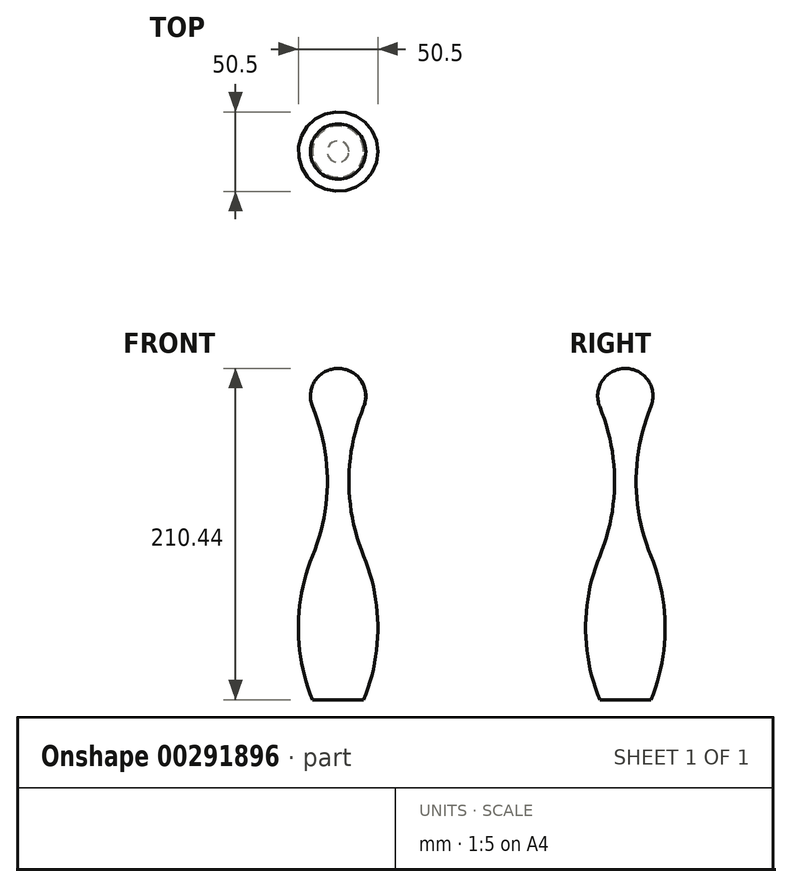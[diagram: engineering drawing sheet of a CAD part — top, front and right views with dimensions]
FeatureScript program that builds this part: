
annotation { "Feature Type Name" : "Feature", "Feature Type Description" : "" }
export const myFeature = defineFeature(function(context is Context, id is Id, definition is map)
    precondition{}
    {
        {
            var Q0;
            Q0=qCreatedBy(makeId("Front.planeOp"),FACE);
            var sketch = newSketch(context, id + "F0", { "sketchPlane" : qUnion([Q0])});
            skLineSegment(sketch, "E0", {"start": v(0, 0) * mm, "end": v(25, 0) * mm});
            skArc(sketch, "E1", {"start": v(25, 0) * mm, "mid": v(34, 45.6) * mm, "end": v(25, 91.2) * mm});
            skArc(sketch, "E2", {"start": v(25, 186.2) * mm, "mid": v(15.62, 138.7) * mm, "end": v(25, 91.2) * mm});
            skArc(sketch, "E3", {"start": v(25, 186.2) * mm, "mid": v(23.34, 202.66) * mm, "end": v(8.75, 210.44) * mm});
            skLineSegment(sketch, "E4", {"start": v(8.75, 238.09) * mm, "end": v(8.75, -65.92) * mm});
            skSolve(sketch);
        }
        {
            var Q0;
            Q0 = qSketchRegion(id + "F0", true);
            var Q1;
            Q1=sQuery(id+"F0.wireOp",EDGE,"E4");
            revolve(context, id + "F1", {"entities" : qUnion([Q0]), "axis" : qUnion([Q1]), "revolveType" : RevolveType.FULL});
        }
    });
